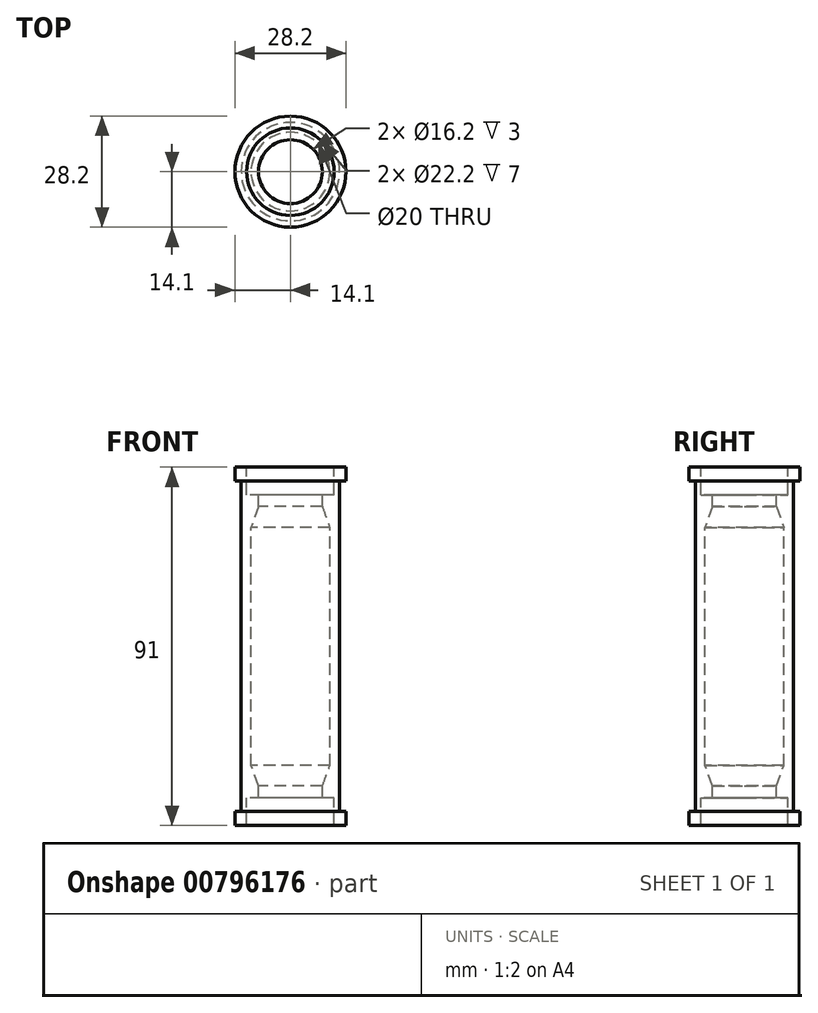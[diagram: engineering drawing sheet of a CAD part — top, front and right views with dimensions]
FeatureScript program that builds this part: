
annotation { "Feature Type Name" : "Feature", "Feature Type Description" : "" }
export const myFeature = defineFeature(function(context is Context, id is Id, definition is map)
    precondition{}
    {
        {
            var Q0;
            Q0=qCreatedBy(makeId("Front.planeOp"),FACE);
            var sketch = newSketch(context, id + "F0", { "sketchPlane" : qUnion([Q0])});
            skLineSegment(sketch, "E0", {"start": v(-50.3, 0) * mm, "end": v(76.21, 0) * mm, "construction": true});
            skLineSegment(sketch, "E1", {"start": v(0, 48.36) * mm, "end": v(0, -57.86) * mm, "construction": true});
            skLineSegment(sketch, "E2", {"start": v(-14.1, 36.5) * mm, "end": v(-11.1, 36.5) * mm});
            skLineSegment(sketch, "E3", {"start": v(-11.1, 36.5) * mm, "end": v(-11.1, 29.5) * mm});
            skLineSegment(sketch, "E4", {"start": v(-11.1, 29.5) * mm, "end": v(-8.1, 29.5) * mm});
            skLineSegment(sketch, "E5", {"start": v(-8.1, 29.5) * mm, "end": v(-8.1, -47.5) * mm});
            skLineSegment(sketch, "E6", {"start": v(-8.1, -47.5) * mm, "end": v(-11.1, -47.5) * mm});
            skLineSegment(sketch, "E7", {"start": v(-11.1, -47.5) * mm, "end": v(-11.1, -54.5) * mm});
            skLineSegment(sketch, "E8", {"start": v(-11.1, -54.5) * mm, "end": v(-14.1, -54.5) * mm});
            skLineSegment(sketch, "E9", {"start": v(-14.1, -54.5) * mm, "end": v(-14.1, -51) * mm});
            skLineSegment(sketch, "E10", {"start": v(-14.1, -51) * mm, "end": v(-12.5, -51) * mm});
            skLineSegment(sketch, "E11", {"start": v(-12.5, -51) * mm, "end": v(-12.5, 33) * mm});
            skLineSegment(sketch, "E12", {"start": v(-12.5, 33) * mm, "end": v(-14.1, 33) * mm});
            skLineSegment(sketch, "E13", {"start": v(-14.1, 33) * mm, "end": v(-14.1, 36.5) * mm});
            skSolve(sketch);
        }
        {
            var Q0;
            Q0=makeQuery(id+"F0.imprint","IMPRINT",FACE,{"disambiguationData":[TD([[makeQuery(id+"F0.imprint","IMPRINT",EDGE,{"derivedFrom":sQuery(id+"F0.wireOp",EDGE,"E2")}),-1.0]])]});
            var Q1;
            Q1=sQuery(id+"F0.wireOp",EDGE,"E1");
            revolve(context, id + "F1", {"surfaceOperationType" : NewSurfaceOperationType.NEW, "entities" : qUnion([Q0]), "axis" : qUnion([Q1]), "revolveType" : RevolveType.FULL});
        }
        {
            var Q0;
            Q0=qCreatedBy(makeId("Front.planeOp"),FACE);
            var sketch = newSketch(context, id + "F2", { "sketchPlane" : qUnion([Q0])});
            skLineSegment(sketch, "E14", {"start": v(-8.1, 26.5) * mm, "end": v(-10, 21.14) * mm});
            skLineSegment(sketch, "E15", {"start": v(-10, 21.14) * mm, "end": v(-10, -39.32) * mm});
            skLineSegment(sketch, "E16", {"start": v(-10, -39.32) * mm, "end": v(-8.1, -44.5) * mm});
            skLineSegment(sketch, "E17", {"start": v(-8.1, -44.5) * mm, "end": v(-8.1, 26.5) * mm});
            skSolve(sketch);
        }
        {
            var Q0;
            Q0 = qSketchRegion(id + "F2", true);
            var Q1;
            Q1=makeQuery(id+"F1.opRevolve","SWEPT_EDGE",EDGE,{"disambiguationData":[OSD([sQuery(id+"F0.wireOp",EDGE,"E4"),sQuery(id+"F0.wireOp",EDGE,"E5")])]});
            revolve(context, id + "F3", {"operationType" : NewBodyOperationType.REMOVE, "surfaceOperationType" : NewSurfaceOperationType.NEW, "entities" : qUnion([Q0]), "axis" : qUnion([Q1]), "revolveType" : RevolveType.FULL, "oppositeDirection" : true});
        }
    });
